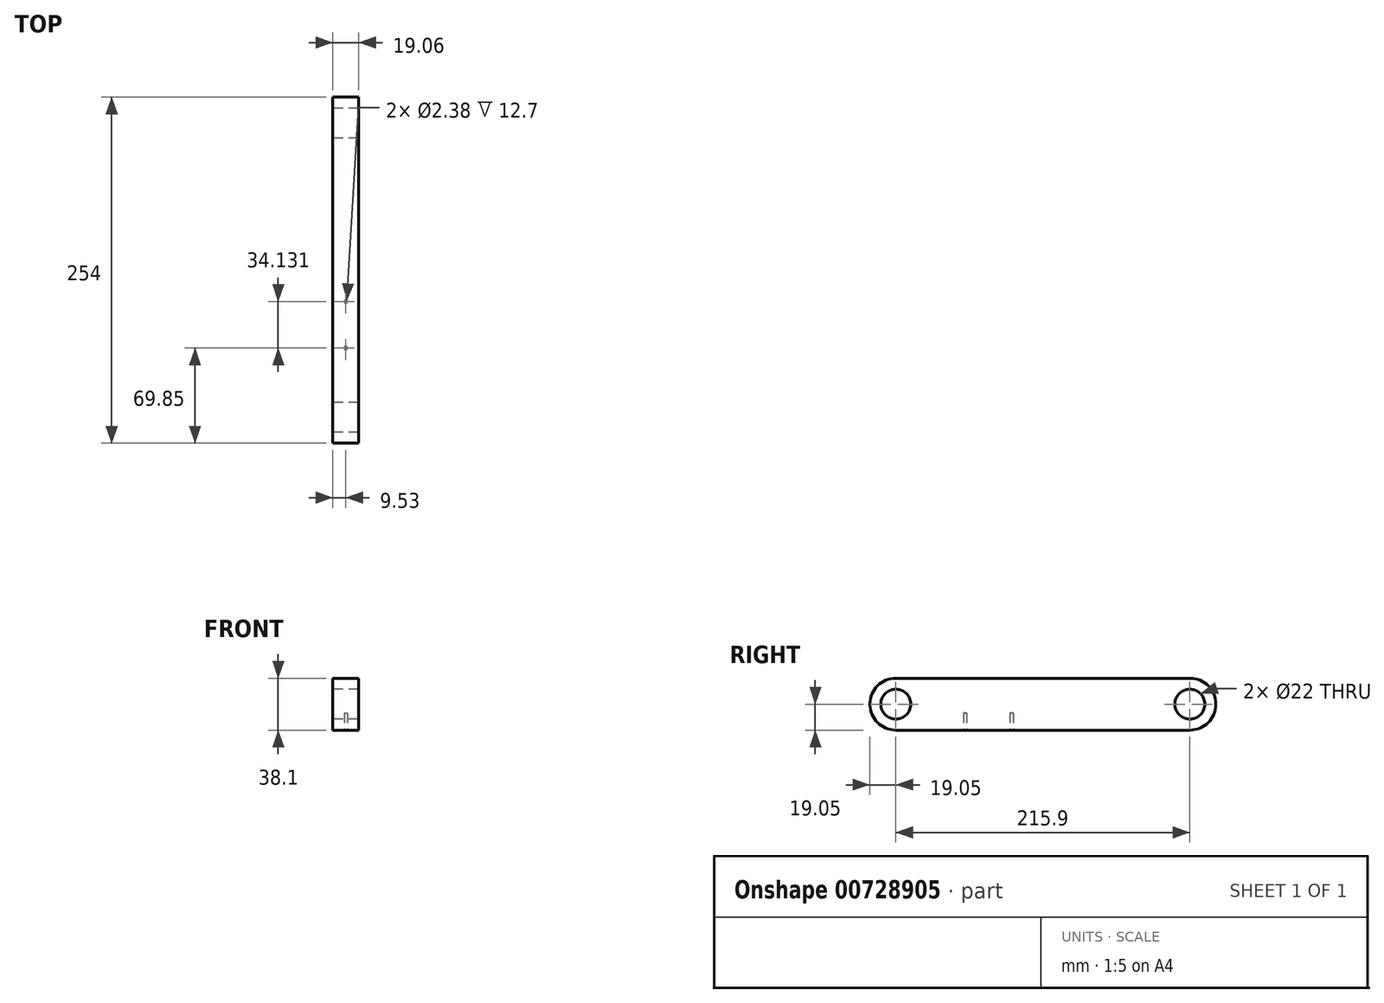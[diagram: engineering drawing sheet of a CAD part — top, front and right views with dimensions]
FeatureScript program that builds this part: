
annotation { "Feature Type Name" : "Feature", "Feature Type Description" : "" }
export const myFeature = defineFeature(function(context is Context, id is Id, definition is map)
    precondition{}
    {
        {
            var Q0;
            Q0=qCreatedBy(makeId("Front.planeOp"),FACE);
            var sketch = newSketch(context, id + "F0", { "sketchPlane" : qUnion([Q0])});
            skLineSegment(sketch, "E0.bottom", {"start": v(9.53, -19.05) * mm, "end": v(-9.53, -19.05) * mm});
            skLineSegment(sketch, "E0.top", {"start": v(9.53, 19.05) * mm, "end": v(-9.52, 19.05) * mm});
            skLineSegment(sketch, "E0.left", {"start": v(9.53, -19.05) * mm, "end": v(9.53, 19.05) * mm});
            skLineSegment(sketch, "E0.right", {"start": v(-9.53, -19.05) * mm, "end": v(-9.52, 19.05) * mm});
            skPoint(sketch, "E0.middle", {"position": v(0, 0) * mm});
            skSolve(sketch);
        }
        {
            var Q0;
            Q0=makeQuery(id+"F0.imprint","IMPRINT",FACE,{"disambiguationData":[TD([[makeQuery(id+"F0.imprint","IMPRINT",EDGE,{"derivedFrom":sQuery(id+"F0.wireOp",EDGE,"E0.bottom")}),-1.0]])]});
            extrude(context, id + "F1", {"entities" : qUnion([Q0]), "oppositeDirection" : true, "depth" : 254 * mm, "offsetDistance" : 25.4 * mm});
        }
        {
            var Q0;
            Q0=makeQuery(id+"F1.opExtrude","SWEPT_FACE",FACE,{"disambiguationData":[OSD([sQuery(id+"F0.wireOp",EDGE,"E0.left")])]});
            var sketch = newSketch(context, id + "F2", { "sketchPlane" : qUnion([Q0])});
            skPoint(sketch, "E1", {"position": v(19.05, 0) * mm});
            skPoint(sketch, "E2", {"position": v(234.95, 0) * mm});
            skSolve(sketch);
        }
        {
            var Q0;
            Q0=sQuery(id+"F2.wireOp",VERTEX,"E1");
            var Q1;
            Q1=sQuery(id+"F2.wireOp",VERTEX,"E2");
            var Q2;
            Q2=makeQuery(id+"F1.opExtrude","SWEPT_BODY",BODY,{"disambiguationData":[OSD([sQuery(id+"F0.wireOp",EDGE,"E0.bottom"),sQuery(id+"F0.wireOp",EDGE,"E0.top"),sQuery(id+"F0.wireOp",EDGE,"E0.left"),sQuery(id+"F0.wireOp",EDGE,"E0.right")])]});
            hole(context, id + "F3", {"style" : HoleStyle.SIMPLE, "endStyle" : HoleEndStyle.THROUGH, "holeDiameter" : 22 * mm, "majorDiameter" : 6.35 * mm, "isTappedThrough" : true, "tappedDepth" : 13.5 * mm, "tapClearance" : 3, "locations" : qUnion([Q0, Q1]), "scope" : qUnion([Q2]), "startStyle" : HoleStartStyle.PART});
        }
        {
            var Q0;
            Q0=makeQuery(id+"F1.opExtrude","CAP_EDGE",EDGE,{"disambiguationData":[OSD([sQuery(id+"F0.wireOp",EDGE,"E0.top")])],"isStart":true});
            var Q1;
            Q1=makeQuery(id+"F1.opExtrude","CAP_EDGE",EDGE,{"disambiguationData":[OSD([sQuery(id+"F0.wireOp",EDGE,"E0.bottom")])],"isStart":true});
            var Q2;
            Q2=makeQuery(id+"F1.opExtrude","CAP_EDGE",EDGE,{"disambiguationData":[OSD([sQuery(id+"F0.wireOp",EDGE,"E0.top")])],"isStart":false});
            var Q3;
            Q3=makeQuery(id+"F1.opExtrude","CAP_EDGE",EDGE,{"disambiguationData":[OSD([sQuery(id+"F0.wireOp",EDGE,"E0.bottom")])],"isStart":false});
            fillet(context, id + "F4", {"entities" : qUnion([Q0, Q1, Q2, Q3]), "radius" : 19.05 * mm, "tangentPropagation" : true, "allowEdgeOverflow" : false});
        }
        {
            var Q0;
            Q0=makeQuery(id+"F1.opExtrude","SWEPT_FACE",FACE,{"disambiguationData":[OSD([sQuery(id+"F0.wireOp",EDGE,"E0.bottom")])]});
            var sketch = newSketch(context, id + "F5", { "sketchPlane" : qUnion([Q0])});
            skCircle(sketch, "E3", {"center": v(0, -69.85) * mm, "radius": 1.2 * mm});
            skCircle(sketch, "E4", {"center": v(0, -103.98) * mm, "radius": 1.2 * mm});
            skSolve(sketch);
        }
        {
            var Q0;
            Q0=makeQuery(id+"F5.imprint","IMPRINT",FACE,{"disambiguationData":[TD([[makeQuery(id+"F5.imprint","IMPRINT",EDGE,{"derivedFrom":sQuery(id+"F5.wireOp",EDGE,"E4")}),1.0]])]});
            var Q1;
            Q1=makeQuery(id+"F5.imprint","IMPRINT",FACE,{"disambiguationData":[TD([[makeQuery(id+"F5.imprint","IMPRINT",EDGE,{"derivedFrom":sQuery(id+"F5.wireOp",EDGE,"E3")}),1.0]])]});
            extrude(context, id + "F6", {"entities" : qUnion([Q0, Q1]), "operationType" : NewBodyOperationType.REMOVE, "oppositeDirection" : true, "depth" : 12.7 * mm, "offsetDistance" : 25.4 * mm});
        }
    });
